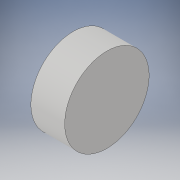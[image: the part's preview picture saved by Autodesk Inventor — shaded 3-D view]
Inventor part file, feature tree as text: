
AUTODESK INVENTOR PART (.ipt)
format: ipt  version: 2019 (Build 230136000, 136)  size: 89,600 bytes
history: native  units: in
note: dims shown in document units (in); Inventor stores cm internally (conversion verified against a paired STEP export)
features: extrude x1, sketch x1
ambient origin geometry x8: Origin, YZ Plane, XZ Plane, XY Plane, X Axis, Y Axis, Z Axis, Center Point
bodies: Solid1 (feature_tree)
feature tree (2):
  extrude  "Extrusion1"  Depth=1.0in TaperAngle=0.0deg
  sketch  "Sketch1"  dims[d0=2.5in d1=1.0in d2=0.0in]
